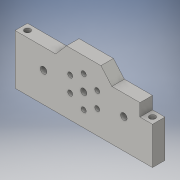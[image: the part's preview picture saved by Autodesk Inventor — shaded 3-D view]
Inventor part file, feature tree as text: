
AUTODESK INVENTOR PART (.ipt)
format: ipt  version: 2016 (Build 200138000, 138)  size: 370,688 bytes
history: native  units: mm
features: projected_geometry x8, extrude x6, other x4, sketch x4, fillet x2, hole x1
ambient origin geometry x8: Origin, YZ Plane, XZ Plane, XY Plane, X Axis, Y Axis, Z Axis, Center Point
bodies: Body1 (feature_tree)
feature tree (25):
  other  "構築線"
  extrude  "押し出し11"  Depth=17.0mm
  other  "固定穴"
  extrude  "押し出し19"  Depth=5.6mm
  extrude  "押し出し21"  Depth=10.0mm
  other  "ねじ穴+固定(基板)"
  hole  "ねじ穴(基板)"  [1 undecoded]
  extrude  "押し出し22"  Depth=10.0mm
  fillet  "フィレット1"  [1 undecoded]
  fillet  "フィレット2"  Radius=20.1mm
  extrude  "押し出し28"  TaperAngle=0.0deg  [1 undecoded]
  other  "外形上面(dxf出力用)"
  sketch  "スケッチ25"
  sketch  "スケッチ27"
  extrude  "押し出し29"  Depth=25.0mm
  sketch  "スケッチ20"
  projected_geometry  "投影ループ4"
  projected_geometry  "投影ループ5"
  projected_geometry  "投影ループ6"
  projected_geometry  "投影ループ7"
  projected_geometry  "投影ループ8"
  projected_geometry  "投影ループ13"
  projected_geometry  "投影ループ14"
  projected_geometry  "投影ループ16"
  sketch  "スケッチ29"
note: 3 required parameter values undecoded (feature->parameter linkage not recoverable at this tier; creation-order binding heuristic only, values carry confidence <= 0.55)
